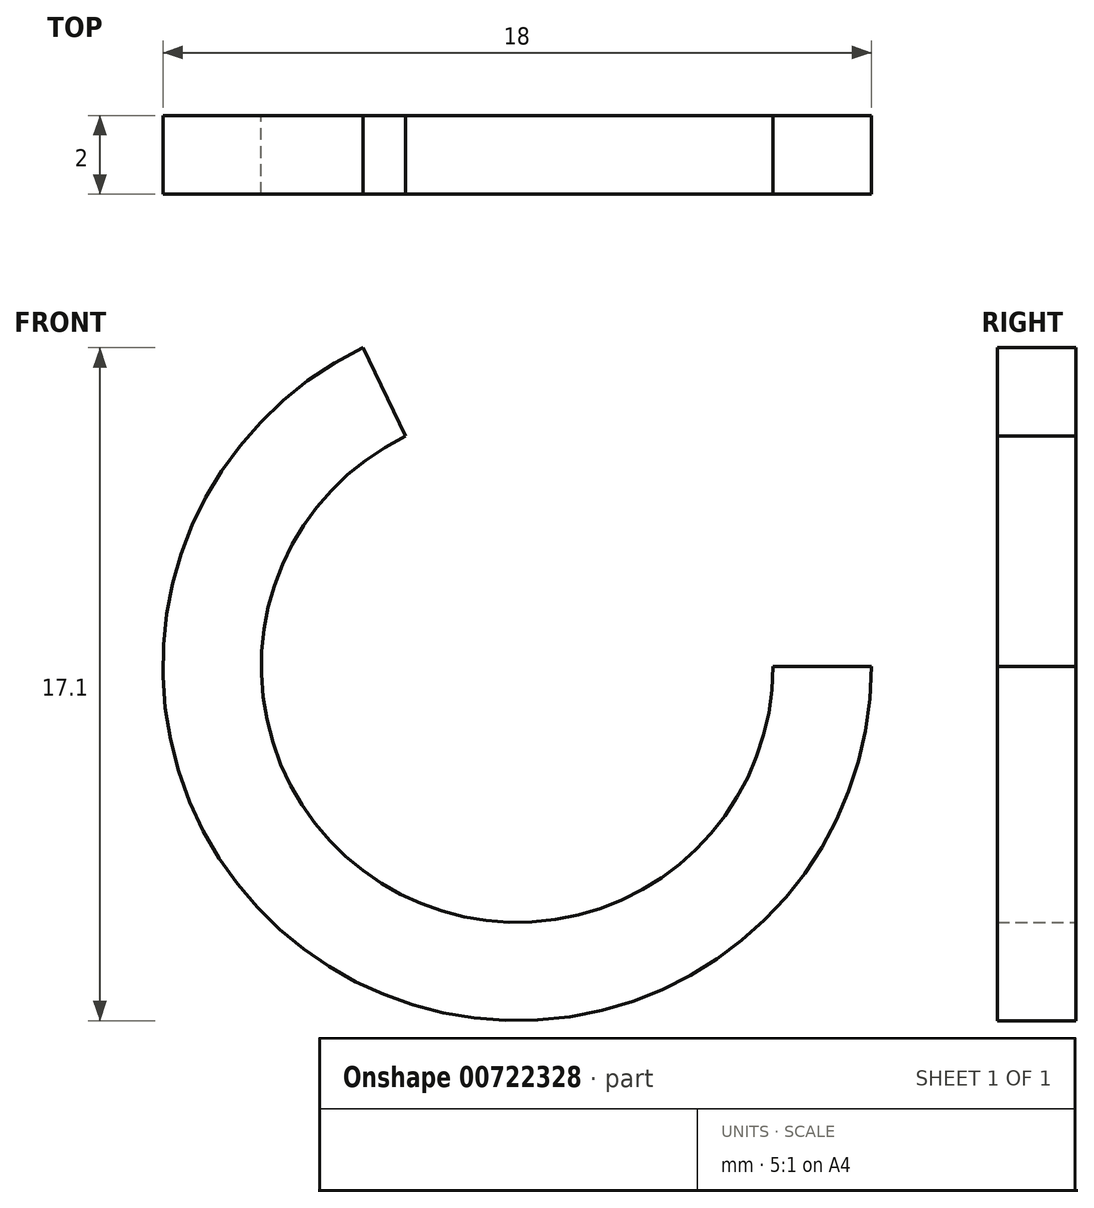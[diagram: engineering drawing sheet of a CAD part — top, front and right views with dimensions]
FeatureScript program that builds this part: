
annotation { "Feature Type Name" : "Feature", "Feature Type Description" : "" }
export const myFeature = defineFeature(function(context is Context, id is Id, definition is map)
    precondition{}
    {
        {
            var Q0;
            Q0=qCreatedBy(makeId("Front.planeOp"),FACE);
            var sketch = newSketch(context, id + "F0", { "sketchPlane" : qUnion([Q0])});
            skArc(sketch, "E0", {"start": v(-3.92, 8.1) * mm, "mid": v(-4.78, -7.62) * mm, "end": v(9, 0) * mm});
            skArc(sketch, "E1", {"start": v(-2.84, 5.85) * mm, "mid": v(-3.45, -5.5) * mm, "end": v(6.5, 0) * mm});
            skLineSegment(sketch, "E2", {"start": v(6.5, 0) * mm, "end": v(9, 0) * mm});
            skLineSegment(sketch, "E3", {"start": v(-2.84, 5.85) * mm, "end": v(-3.92, 8.1) * mm});
            skSolve(sketch);
        }
        {
            var Q0;
            Q0=makeQuery(id+"F0.imprint","IMPRINT",FACE,{"disambiguationData":[TD([[makeQuery(id+"F0.imprint","IMPRINT",EDGE,{"derivedFrom":sQuery(id+"F0.wireOp",EDGE,"E0")}),1.0]])]});
            extrude(context, id + "F1", {"entities" : qUnion([Q0]), "depth" : 2 * mm, "offsetDistance" : 25 * mm});
        }
    });
